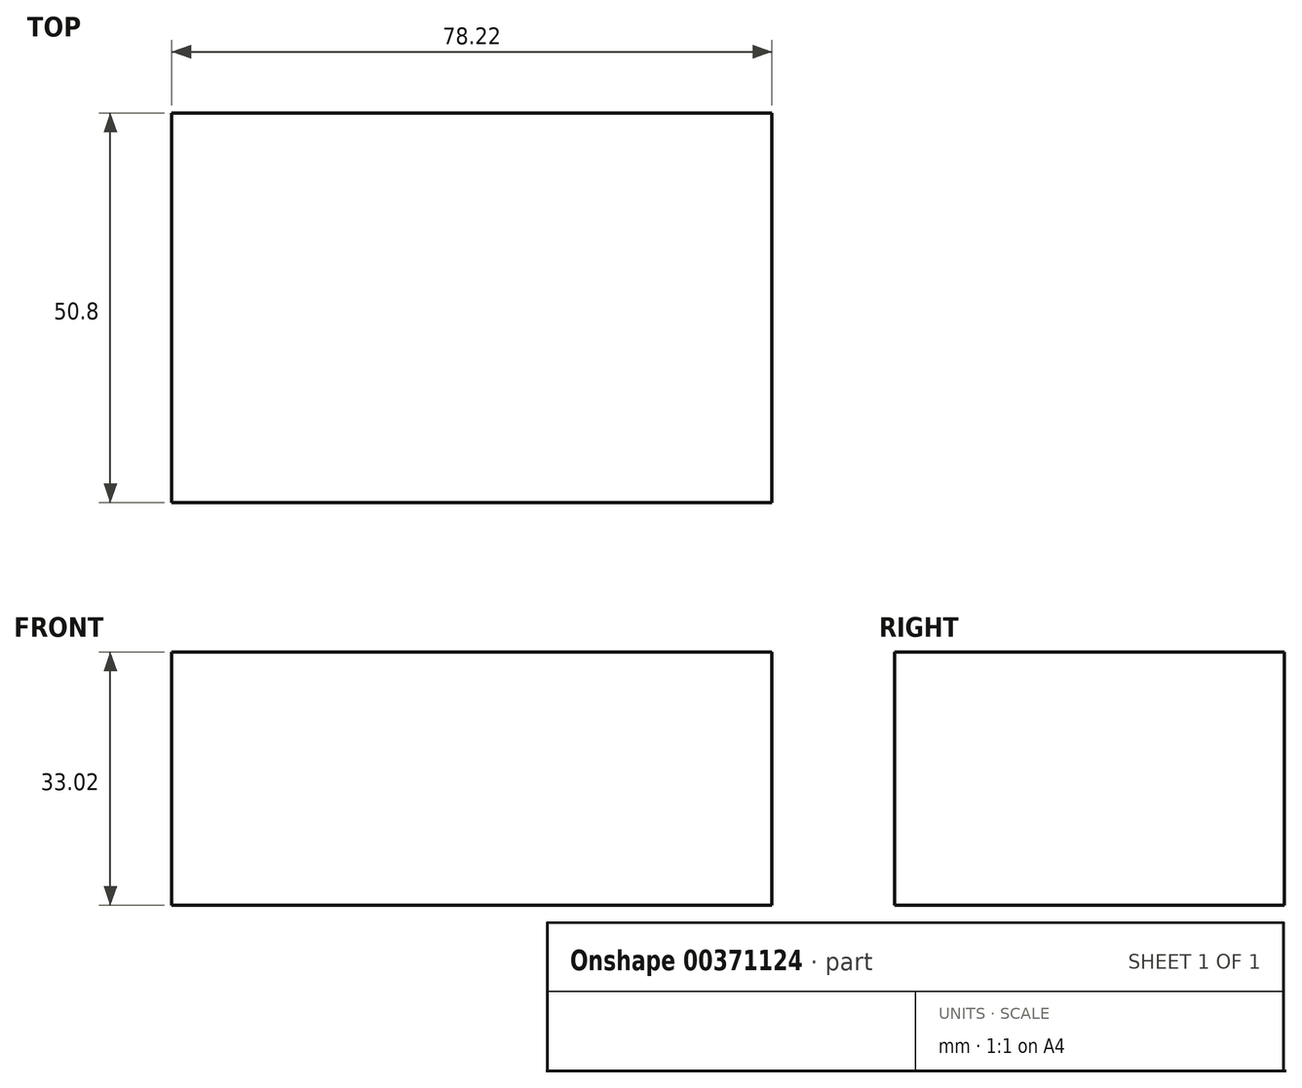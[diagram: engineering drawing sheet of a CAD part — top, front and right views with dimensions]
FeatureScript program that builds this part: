
annotation { "Feature Type Name" : "Feature", "Feature Type Description" : "" }
export const myFeature = defineFeature(function(context is Context, id is Id, definition is map)
    precondition{}
    {
        {
            var Q0;
            Q0=qCreatedBy(makeId("Front.planeOp"),FACE);
            var sketch = newSketch(context, id + "F0", { "sketchPlane" : qUnion([Q0])});
            skLineSegment(sketch, "E0.bottom", {"start": v(0, 0) * mm, "end": v(52.82, 0) * mm});
            skLineSegment(sketch, "E0.top", {"start": v(0, 33.02) * mm, "end": v(52.82, 33.02) * mm});
            skLineSegment(sketch, "E0.left", {"start": v(0, 0) * mm, "end": v(0, 33.02) * mm});
            skLineSegment(sketch, "E0.right", {"start": v(52.82, 0) * mm, "end": v(52.82, 33.02) * mm});
            skSolve(sketch);
        }
        {
            var Q0;
            Q0=makeQuery(id+"F0.imprint","IMPRINT",FACE,{"disambiguationData":[TD([[makeQuery(id+"F0.imprint","IMPRINT",EDGE,{"derivedFrom":sQuery(id+"F0.wireOp",EDGE,"E0.bottom")}),1.0]])]});
            extrude(context, id + "F1", {"entities" : qUnion([Q0]), "depth" : 50.8 * mm});
        }
        {
            var Q0;
            Q0=makeQuery(id+"F1.opExtrude","SWEPT_FACE",FACE,{"disambiguationData":[OSD([sQuery(id+"F0.wireOp",EDGE,"E0.left")])]});
            var sketch = newSketch(context, id + "F2", { "sketchPlane" : qUnion([Q0])});
            skCircle(sketch, "E1", {"center": v(77.7, 104.64) * mm, "radius": 22.35 * mm});
            skSolve(sketch);
        }
        {
            var Q0;
            {var subQ0=sQuery(id+"F0.wireOp",EDGE,"E0.left");Q0=makeQuery(id+"F2.imprint","IMPRINT",FACE,{"disambiguationData":[TD([[makeQuery(id+"F2.imprint","IMPRINT",EDGE,{"derivedFrom":makeQuery(id+"F1.opExtrude","CAP_EDGE",EDGE,{"disambiguationData":[OSD([subQ0])],"isStart":true})}),-1.0]])]});}
            extrude(context, id + "F3", {"entities" : qUnion([Q0]), "operationType" : NewBodyOperationType.ADD, "depth" : 25.4 * mm});
        }
    });
